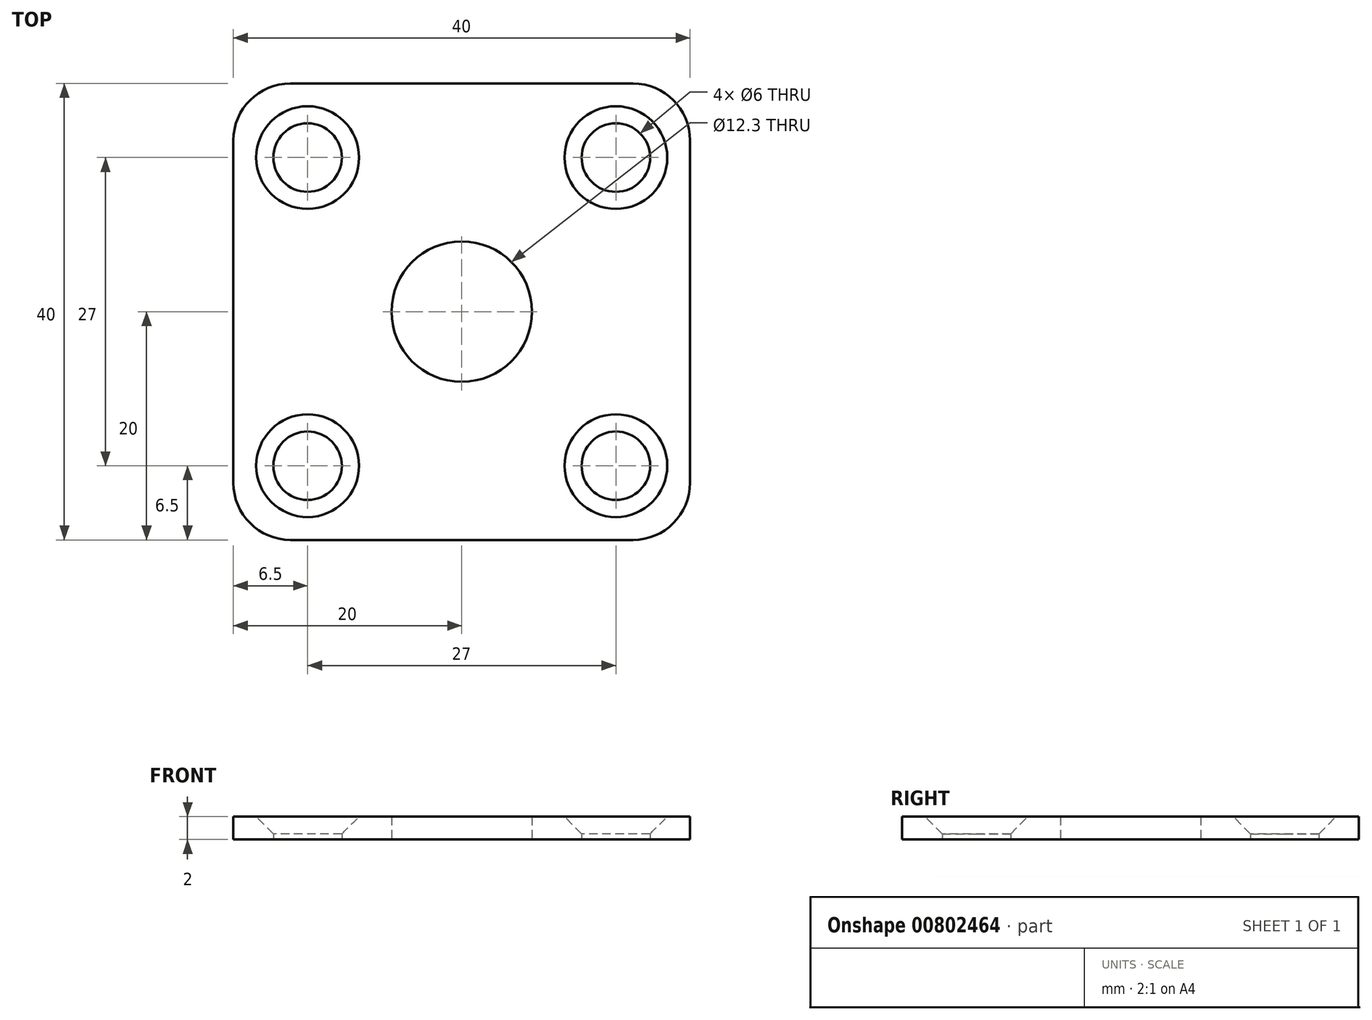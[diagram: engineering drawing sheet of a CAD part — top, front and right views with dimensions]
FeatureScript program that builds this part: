
annotation { "Feature Type Name" : "Feature", "Feature Type Description" : "" }
export const myFeature = defineFeature(function(context is Context, id is Id, definition is map)
    precondition{}
    {
        {
            var Q0;
            Q0=qCreatedBy(makeId("Top.planeOp"),FACE);
            var sketch = newSketch(context, id + "F0", { "sketchPlane" : qUnion([Q0])});
            skCircle(sketch, "E0", {"center": v(0, 0) * mm, "radius": 11.2 * mm});
            skCircle(sketch, "E1", {"center": v(0, 0) * mm, "radius": 6.15 * mm});
            skLineSegment(sketch, "E2.bottom", {"start": v(20, -20) * mm, "end": v(-20, -20) * mm});
            skLineSegment(sketch, "E2.top", {"start": v(20, 20) * mm, "end": v(-20, 20) * mm});
            skLineSegment(sketch, "E2.left", {"start": v(20, -20) * mm, "end": v(20, 20) * mm});
            skLineSegment(sketch, "E2.right", {"start": v(-20, -20) * mm, "end": v(-20, 20) * mm});
            skLineSegment(sketch, "E3.bottom", {"start": v(13.5, -13.5) * mm, "end": v(-13.5, -13.5) * mm, "construction": true});
            skLineSegment(sketch, "E3.top", {"start": v(13.5, 13.5) * mm, "end": v(-13.5, 13.5) * mm, "construction": true});
            skLineSegment(sketch, "E3.left", {"start": v(13.5, -13.5) * mm, "end": v(13.5, 13.5) * mm, "construction": true});
            skLineSegment(sketch, "E3.right", {"start": v(-13.5, -13.5) * mm, "end": v(-13.5, 13.5) * mm, "construction": true});
            skCircle(sketch, "E4", {"center": v(-13.5, 13.5) * mm, "radius": 3 * mm});
            skCircle(sketch, "E5", {"center": v(-13.5, -13.5) * mm, "radius": 3 * mm});
            skCircle(sketch, "E6", {"center": v(13.5, 13.5) * mm, "radius": 3 * mm});
            skCircle(sketch, "E7", {"center": v(13.5, -13.5) * mm, "radius": 3 * mm});
            skSolve(sketch);
        }
        {
            var Q0;
            Q0=makeQuery(id+"F0.imprint","IMPRINT",FACE,{"disambiguationData":[TD([[makeQuery(id+"F0.imprint","IMPRINT",EDGE,{"derivedFrom":sQuery(id+"F0.wireOp",EDGE,"E0")}),-1.0]])]});
            var Q1;
            Q1=makeQuery(id+"F0.imprint","IMPRINT",FACE,{"disambiguationData":[TD([[makeQuery(id+"F0.imprint","IMPRINT",EDGE,{"derivedFrom":sQuery(id+"F0.wireOp",EDGE,"E0")}),1.0]])]});
            extrude(context, id + "F1", {"entities" : qUnion([Q0, Q1]), "depth" : 2 * mm, "offsetDistance" : 25 * mm});
        }
        {
            var Q0;
            Q0=makeQuery(id+"F1.opExtrude","SWEPT_EDGE",EDGE,{"disambiguationData":[OSD([sQuery(id+"F0.wireOp",EDGE,"E2.bottom"),sQuery(id+"F0.wireOp",EDGE,"E2.right")])]});
            var Q1;
            Q1=makeQuery(id+"F1.opExtrude","SWEPT_EDGE",EDGE,{"disambiguationData":[OSD([sQuery(id+"F0.wireOp",EDGE,"E2.bottom"),sQuery(id+"F0.wireOp",EDGE,"E2.left")])]});
            var Q2;
            Q2=makeQuery(id+"F1.opExtrude","SWEPT_EDGE",EDGE,{"disambiguationData":[OSD([sQuery(id+"F0.wireOp",EDGE,"E2.top"),sQuery(id+"F0.wireOp",EDGE,"E2.left")])]});
            var Q3;
            Q3=makeQuery(id+"F1.opExtrude","SWEPT_EDGE",EDGE,{"disambiguationData":[OSD([sQuery(id+"F0.wireOp",EDGE,"E2.top"),sQuery(id+"F0.wireOp",EDGE,"E2.right")])]});
            fillet(context, id + "F2", {"entities" : qUnion([Q0, Q1, Q2, Q3]), "radius" : 5 * mm, "tangentPropagation" : true, "allowEdgeOverflow" : false});
        }
        {
            var Q0;
            Q0=makeQuery(id+"F1.opExtrude","CAP_EDGE",EDGE,{"disambiguationData":[OSD([sQuery(id+"F0.wireOp",EDGE,"E4")])],"isStart":false});
            var Q1;
            Q1=makeQuery(id+"F1.opExtrude","CAP_EDGE",EDGE,{"disambiguationData":[OSD([sQuery(id+"F0.wireOp",EDGE,"E5")])],"isStart":false});
            var Q2;
            Q2=makeQuery(id+"F1.opExtrude","CAP_EDGE",EDGE,{"disambiguationData":[OSD([sQuery(id+"F0.wireOp",EDGE,"E6")])],"isStart":false});
            var Q3;
            Q3=makeQuery(id+"F1.opExtrude","CAP_EDGE",EDGE,{"disambiguationData":[OSD([sQuery(id+"F0.wireOp",EDGE,"E7")])],"isStart":false});
            chamfer(context, id + "F3", {"entities" : qUnion([Q0, Q1, Q2, Q3]), "width" : 1.5 * mm, "tangentPropagation" : true});
        }
    });
